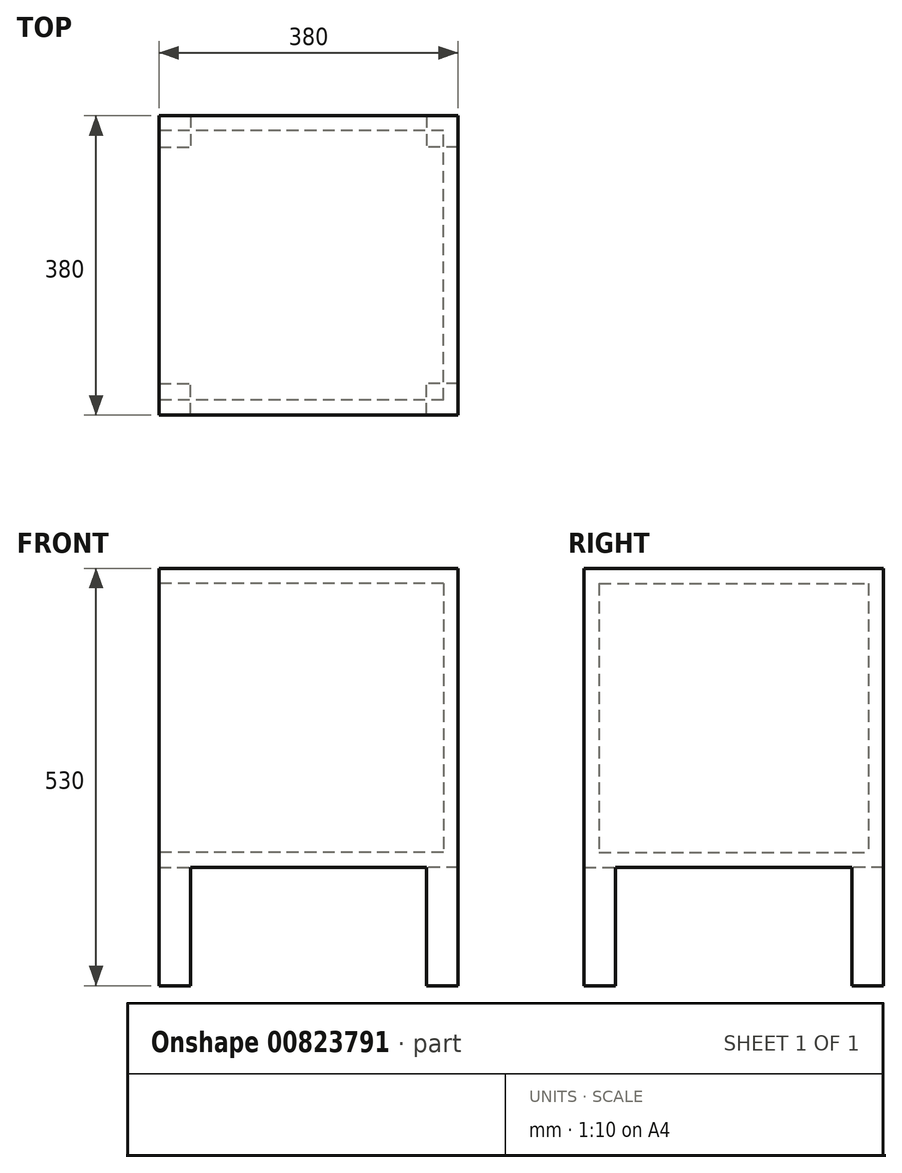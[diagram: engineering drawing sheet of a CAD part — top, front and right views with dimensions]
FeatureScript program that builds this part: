
annotation { "Feature Type Name" : "Feature", "Feature Type Description" : "" }
export const myFeature = defineFeature(function(context is Context, id is Id, definition is map)
    precondition{}
    {
        {
            var Q0;
            Q0=qCreatedBy(makeId("Top.planeOp"),FACE);
            var sketch = newSketch(context, id + "F0", { "sketchPlane" : qUnion([Q0])});
            skLineSegment(sketch, "E0.bottom", {"start": v(-190, 190) * mm, "end": v(190, 190) * mm});
            skLineSegment(sketch, "E0.top", {"start": v(-190, -190) * mm, "end": v(190, -190) * mm});
            skLineSegment(sketch, "E0.left", {"start": v(-190, 190) * mm, "end": v(-190, -190) * mm});
            skLineSegment(sketch, "E0.right", {"start": v(190, 190) * mm, "end": v(190, -190) * mm});
            skPoint(sketch, "E0.middle", {"position": v(0, 0) * mm});
            skSolve(sketch);
        }
        {
            var Q0;
            Q0 = qSketchRegion(id + "F0", true);
            extrude(context, id + "F1", {"entities" : qUnion([Q0]), "depth" : 380 * mm, "offsetDistance" : 25 * mm});
        }
        {
            var Q0;
            Q0=makeQuery(id+"F1.opExtrude","SWEPT_FACE",FACE,{"disambiguationData":[OSD([sQuery(id+"F0.wireOp",EDGE,"E0.left")])]});
            var sketch = newSketch(context, id + "F2", { "sketchPlane" : qUnion([Q0])});
            skLineSegment(sketch, "E1.bottom", {"start": v(171, 361) * mm, "end": v(-171, 361) * mm});
            skLineSegment(sketch, "E1.top", {"start": v(171, 19) * mm, "end": v(-171, 19) * mm});
            skLineSegment(sketch, "E1.left", {"start": v(171, 361) * mm, "end": v(171, 19) * mm});
            skLineSegment(sketch, "E1.right", {"start": v(-171, 361) * mm, "end": v(-171, 19) * mm});
            skPoint(sketch, "E1.middle", {"position": v(0, 190) * mm});
            skPoint(sketch, "E1.middle.positionSnap0", {"position": v(190, 190) * mm});
            skPoint(sketch, "E1.centerSnap0", {"position": v(190, 190) * mm});
            skSolve(sketch);
        }
        {
            var Q0;
            Q0 = qSketchRegion(id + "F2", true);
            extrude(context, id + "F3", {"entities" : qUnion([Q0]), "operationType" : NewBodyOperationType.REMOVE, "oppositeDirection" : true, "depth" : 361 * mm, "offsetDistance" : 25 * mm});
        }
        {
            var Q0;
            Q0=makeQuery(id+"F1.opExtrude","CAP_FACE",FACE,{"disambiguationData":[OSD([sQuery(id+"F0.wireOp",EDGE,"E0.bottom"),sQuery(id+"F0.wireOp",EDGE,"E0.top"),sQuery(id+"F0.wireOp",EDGE,"E0.left"),sQuery(id+"F0.wireOp",EDGE,"E0.right")])],"isStart":true});
            var sketch = newSketch(context, id + "F4", { "sketchPlane" : qUnion([Q0])});
            skLineSegment(sketch, "E2.bottom", {"start": v(190, 190) * mm, "end": v(150, 190) * mm});
            skLineSegment(sketch, "E2.top", {"start": v(190, 150) * mm, "end": v(150, 150) * mm});
            skLineSegment(sketch, "E2.left", {"start": v(190, 190) * mm, "end": v(190, 150) * mm});
            skLineSegment(sketch, "E2.right", {"start": v(150, 190) * mm, "end": v(150, 150) * mm});
            skLineSegment(sketch, "E3.bottom", {"start": v(-190, 190) * mm, "end": v(-150, 190) * mm});
            skLineSegment(sketch, "E3.top", {"start": v(-190, 150) * mm, "end": v(-150, 150) * mm});
            skLineSegment(sketch, "E3.left", {"start": v(-190, 190) * mm, "end": v(-190, 150) * mm});
            skLineSegment(sketch, "E3.right", {"start": v(-150, 190) * mm, "end": v(-150, 150) * mm});
            skLineSegment(sketch, "E4.bottom", {"start": v(-190, -190) * mm, "end": v(-150, -190) * mm});
            skLineSegment(sketch, "E4.top", {"start": v(-190, -150) * mm, "end": v(-150, -150) * mm});
            skLineSegment(sketch, "E4.left", {"start": v(-190, -190) * mm, "end": v(-190, -150) * mm});
            skLineSegment(sketch, "E4.right", {"start": v(-150, -190) * mm, "end": v(-150, -150) * mm});
            skLineSegment(sketch, "E5.bottom", {"start": v(190, -190) * mm, "end": v(150, -190) * mm});
            skLineSegment(sketch, "E5.top", {"start": v(190, -150) * mm, "end": v(150, -150) * mm});
            skLineSegment(sketch, "E5.left", {"start": v(190, -190) * mm, "end": v(190, -150) * mm});
            skLineSegment(sketch, "E5.right", {"start": v(150, -190) * mm, "end": v(150, -150) * mm});
            skSolve(sketch);
        }
        {
            var Q0;
            Q0 = qSketchRegion(id + "F4", true);
            extrude(context, id + "F5", {"entities" : qUnion([Q0]), "operationType" : NewBodyOperationType.ADD, "depth" : 150 * mm, "offsetDistance" : 25 * mm});
        }
    });
